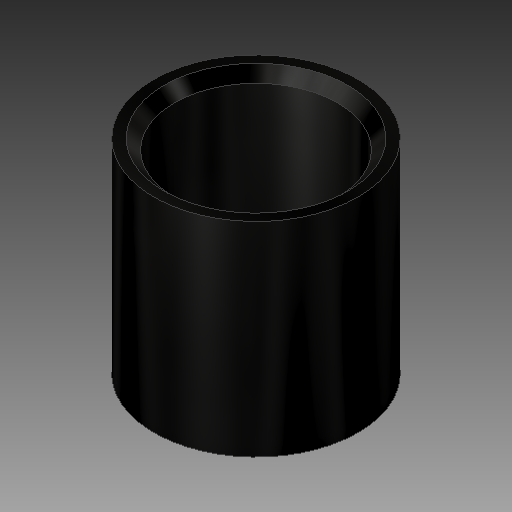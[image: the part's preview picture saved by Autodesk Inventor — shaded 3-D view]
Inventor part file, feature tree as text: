
AUTODESK INVENTOR PART (.ipt)
format: ipt  version: 2019.3 (Build 233278000, 278)  size: 136,704 bytes
history: native  units: mm
features: extrude x1, chamfer x1, sketch x1
ambient origin geometry x8: Origin, YZ Plane, XZ Plane, XY Plane, X Axis, Y Axis, Z Axis, Center Point
bodies: Solid1 (feature_tree)
feature tree (3):
  extrude  "Extrusion1"  Depth=10.0mm
  chamfer  "Chamfer1"  Distance=10.0mm
  sketch  "Sketch1"  dims[d0=8.0mm d1=10.0mm d2=10.0mm d3=0.0mm d4=0.5mm d5=2.0mm d6=45.0deg]
